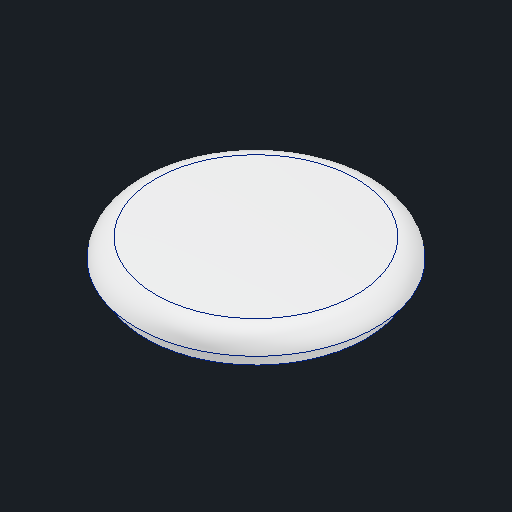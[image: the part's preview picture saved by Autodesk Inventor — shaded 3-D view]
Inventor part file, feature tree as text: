
AUTODESK INVENTOR PART (.ipt)
format: ipt  version: 2025.3 (Build 293356030, 356C)  size: 276,992 bytes
history: native  units: mm
features: sketch x4, extrude x3, other x1, fillet x1, hole x1
ambient origin geometry x8: Origin, YZ Plane, XZ Plane, XY Plane, X Axis, Y Axis, Z Axis, Center Point
bodies: Body1 (feature_tree)
feature tree (10):
  other  "Sólido1"
  sketch  "Boceto1"  dims[d1=8.0mm d2=0.0mm d3=8.0mm d22=4.0mm]
  extrude  "Extrusión1"  Depth=8.0mm
  fillet  "Empalme1"  Radius=4.0mm
  extrude  "Extrusión3"  Depth=6.0mm
  sketch  "Boceto3"  dims[d37=18.0mm d38=5.0mm d39=0.0mm]
  hole  "Agujero2"  [1 undecoded]
  extrude  "Extrusión4"  Depth=5.0mm TaperAngle=0.0deg
  sketch  "Boceto2"  dims[d26=2.459mm d27=8.0mm d28=4.0mm d29=2.0mm d30=90.0deg d31=8.8mm d32=0.0mm d33=60.0mm d35=360.0deg]
  sketch  "Boceto - Patrón circular1"  dims[d23=6.0mm d24=0.0mm d25=37.5mm]
note: 1 required parameter value undecoded (feature->parameter linkage not recoverable at this tier; creation-order binding heuristic only, values carry confidence <= 0.55)
